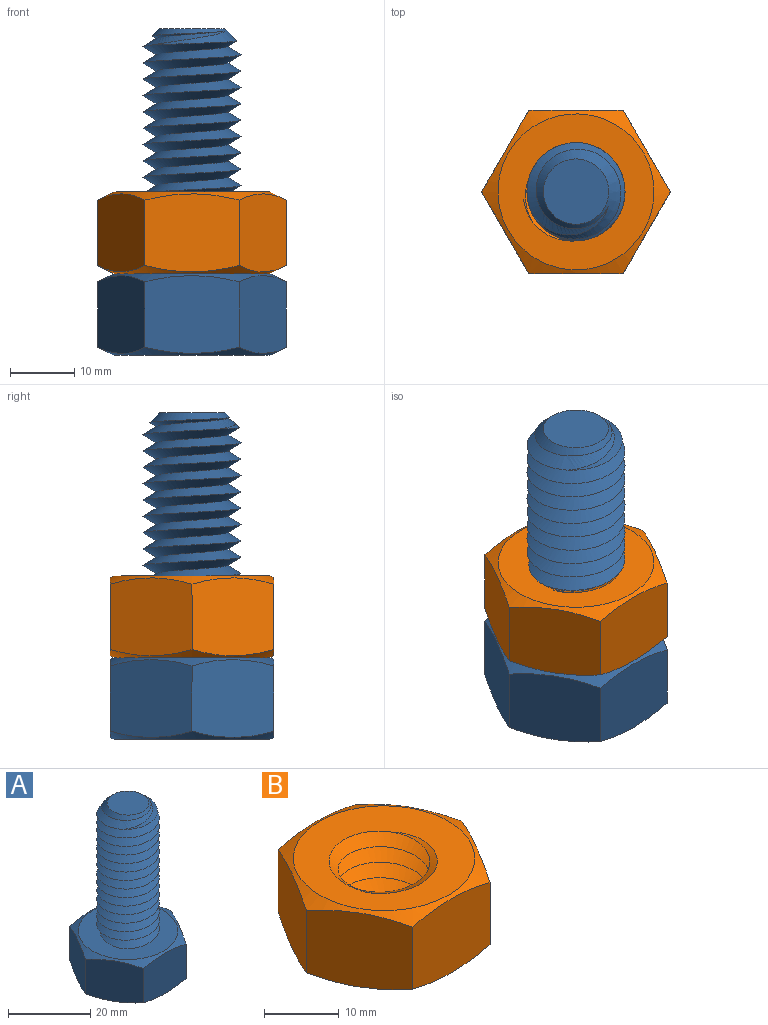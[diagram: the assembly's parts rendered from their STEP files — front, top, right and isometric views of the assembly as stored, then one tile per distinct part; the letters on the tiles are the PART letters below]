
ASSEMBLY  parts=2 mates=1
PART A: 14 faces, bbox 31.1x31.1x53.6 mm
  f0: bspline ~39.37x17.6mm, area 1460mm2, adj f1,f2,f12
  f1: bspline ~40.64x17.6mm, area 1467.6mm2, adj f0,f2,f12
  f2: plane 25.99x25.99mm, normal (0,0,1), area 325.4mm2, adj f0,f1,f3
  f3: cone r=14.66mm half-angle=63.4deg, axis (0,0,-1), area 108.3mm2, adj f2,f4,f5,f6,f7,f8,f9
  f4: plane 14.68x12.13mm, normal (0,-1,0), area 167.9mm2, adj f3,f5,f9,f10
  f5: plane 12.7x12.13mm, normal (0.87,-0.5,0), area 167.9mm2, adj f3,f4,f6,f10
  f6: plane 12.7x12.13mm, normal (0.87,0.5,0), area 167.9mm2, adj f3,f5,f7,f10
  f7: plane 14.68x12.13mm, normal (0,1,0), area 167.9mm2, adj f3,f6,f8,f10
  f8: plane 12.7x12.13mm, normal (-0.87,0.5,0), area 167.9mm2, adj f3,f7,f9,f10
  f9: plane 12.7x12.13mm, normal (-0.87,-0.5,0), area 167.9mm2, adj f3,f4,f8,f10
  f10: cone r=12.12mm half-angle=63.4deg, axis (0,0,1), area 108.3mm2, adj f4,f5,f6,f7,f8,f9,f11
  f11: plane 24.25x24.25mm, normal (0,0,-1), area 461.8mm2, adj f10
  f12: cone r=5.08mm half-angle=45deg, axis (0,0,-1), area 78.4mm2, adj f0,f1,f13
  f13: plane 10.16x10.16mm, normal (0,0,1), area 81.1mm2, adj f12
PART B: 12 faces, bbox 31.1x31.1x17.4 mm
  f0: plane 26x26mm, normal (0,0,1), area 298mm2, adj f1,f10,f11
  f1: cone r=14.66mm half-angle=63.4deg, axis (0,0,-1), area 108.3mm2, adj f0,f2,f3,f4,f5,f6,f7
  f2: plane 14.68x12.13mm, normal (0,-1,0), area 167.9mm2, adj f1,f3,f7,f8
  f3: plane 12.7x12.13mm, normal (-0.87,-0.5,0), area 167.9mm2, adj f1,f2,f4,f8
  f4: plane 12.7x12.13mm, normal (-0.87,0.5,0), area 167.9mm2, adj f1,f3,f5,f8
  f5: plane 14.68x12.13mm, normal (0,1,0), area 167.9mm2, adj f1,f4,f6,f8
  f6: plane 12.7x12.13mm, normal (0.87,0.5,0), area 167.9mm2, adj f1,f5,f7,f8
  f7: plane 12.7x12.13mm, normal (0.87,-0.5,0), area 167.9mm2, adj f1,f2,f6,f8
  f8: cone r=12.12mm half-angle=63.4deg, axis (0,0,1), area 108.3mm2, adj f2,f3,f4,f5,f6,f7,f9
  f9: plane 26x26mm, normal (0,0,-1), area 298mm2, adj f8,f10,f11
  f10: bspline ~19.06x16.51mm, area 558.8mm2, adj f0,f9,f11
  f11: bspline ~19.06x16.51mm, area 558.8mm2, adj f0,f9,f10
PLACE A at identity fixed
PLACE B t=(-38.1,0,12.7)mm
MATE cylindrical A.f3 <-> B.f1  axis (0,0,1) through (0,0,0)mm
